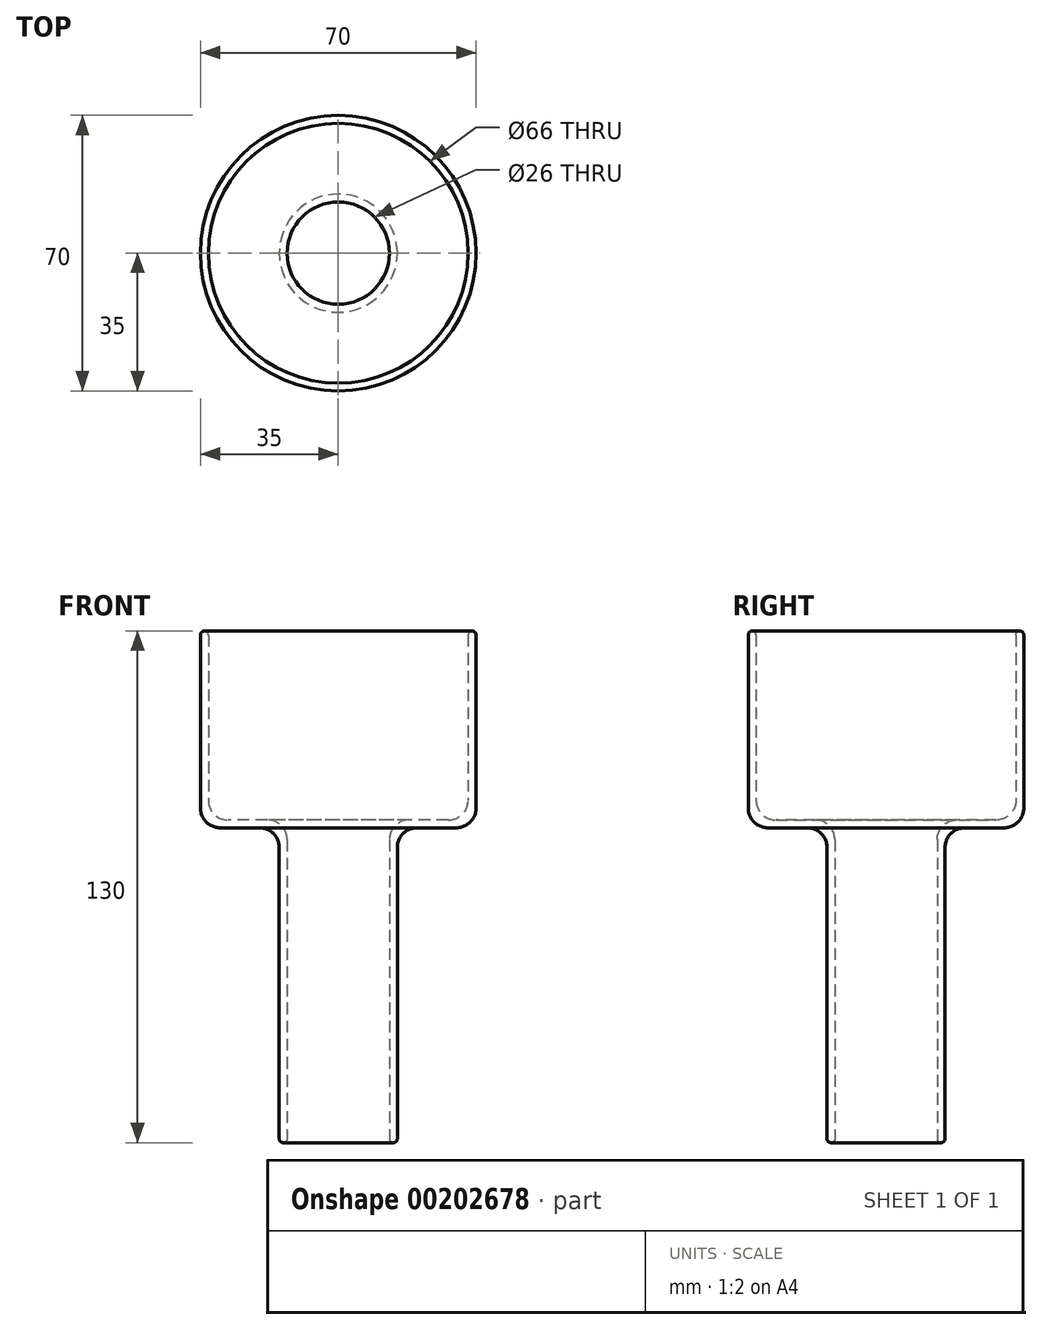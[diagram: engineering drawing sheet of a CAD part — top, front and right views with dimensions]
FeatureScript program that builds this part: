
annotation { "Feature Type Name" : "Feature", "Feature Type Description" : "" }
export const myFeature = defineFeature(function(context is Context, id is Id, definition is map)
    precondition{}
    {
        {
            var Q0;
            Q0=qCreatedBy(makeId("Front.planeOp"),FACE);
            var sketch = newSketch(context, id + "F0", { "sketchPlane" : qUnion([Q0])});
            skLineSegment(sketch, "E0", {"start": v(0, -72.8) * mm, "end": v(0, 57.2) * mm, "construction": true});
            skLineSegment(sketch, "E1", {"start": v(0, 57.2) * mm, "end": v(-35, 57.2) * mm, "construction": true});
            skLineSegment(sketch, "E2", {"start": v(-35, 57.2) * mm, "end": v(-35, 7.2) * mm});
            skLineSegment(sketch, "E3", {"start": v(-35, 7.2) * mm, "end": v(-15, 7.2) * mm});
            skLineSegment(sketch, "E4", {"start": v(-15, 7.2) * mm, "end": v(-15, -72.8) * mm});
            skLineSegment(sketch, "E5", {"start": v(-15, -72.8) * mm, "end": v(0, -72.8) * mm, "construction": true});
            skLineSegment(sketch, "E6.0", {"start": v(-13, 9.2) * mm, "end": v(-13, -72.8) * mm});
            skLineSegment(sketch, "E6.1", {"start": v(-33, 9.2) * mm, "end": v(-13, 9.2) * mm});
            skLineSegment(sketch, "E6.2", {"start": v(-33, 57.2) * mm, "end": v(-33, 9.2) * mm});
            skLineSegment(sketch, "E7", {"start": v(-35, 57.2) * mm, "end": v(-33, 57.2) * mm});
            skLineSegment(sketch, "E8", {"start": v(-15, -72.8) * mm, "end": v(-13, -72.8) * mm});
            skSolve(sketch);
        }
        {
            var Q0;
            Q0 = qSketchRegion(id + "F0", true);
            var Q1;
            Q1=sQuery(id+"F0.wireOp",EDGE,"E0");
            revolve(context, id + "F1", {"entities" : qUnion([Q0]), "axis" : qUnion([Q1]), "revolveType" : RevolveType.FULL});
        }
        {
            var Q0;
            Q0=makeQuery(id+"F1.opRevolve","SWEPT_EDGE",EDGE,{"disambiguationData":[OSD([sQuery(id+"F0.wireOp",EDGE,"E2"),sQuery(id+"F0.wireOp",EDGE,"E7")])]});
            var Q1;
            Q1=makeQuery(id+"F1.opRevolve","SWEPT_EDGE",EDGE,{"disambiguationData":[OSD([sQuery(id+"F0.wireOp",EDGE,"E6.2"),sQuery(id+"F0.wireOp",EDGE,"E7")])]});
            var Q2;
            Q2=makeQuery(id+"F1.opRevolve","SWEPT_FACE",FACE,{"disambiguationData":[OSD([sQuery(id+"F0.wireOp",EDGE,"E8")])]});
            fillet(context, id + "F2", {"entities" : qUnion([Q0, Q1, Q2]), "radius" : 1 * mm, "tangentPropagation" : true, "allowEdgeOverflow" : false});
        }
        {
            var Q0;
            Q0=makeQuery(id+"F1.opRevolve","SWEPT_EDGE",EDGE,{"disambiguationData":[OSD([sQuery(id+"F0.wireOp",EDGE,"E3"),sQuery(id+"F0.wireOp",EDGE,"E4")])]});
            var Q1;
            Q1=makeQuery(id+"F1.opRevolve","SWEPT_EDGE",EDGE,{"disambiguationData":[OSD([sQuery(id+"F0.wireOp",EDGE,"E2"),sQuery(id+"F0.wireOp",EDGE,"E3")])]});
            fillet(context, id + "F3", {"entities" : qUnion([Q0, Q1]), "radius" : 5 * mm, "tangentPropagation" : true, "allowEdgeOverflow" : false});
        }
        {
            var Q0;
            Q0=makeQuery(id+"F1.opRevolve","SWEPT_EDGE",EDGE,{"disambiguationData":[OSD([sQuery(id+"F0.wireOp",EDGE,"E6.0"),sQuery(id+"F0.wireOp",EDGE,"E6.1")])]});
            var Q1;
            Q1=makeQuery(id+"F1.opRevolve","SWEPT_EDGE",EDGE,{"disambiguationData":[OSD([sQuery(id+"F0.wireOp",EDGE,"E6.1"),sQuery(id+"F0.wireOp",EDGE,"E6.2")])]});
            fillet(context, id + "F4", {"entities" : qUnion([Q0, Q1]), "radius" : 5 * mm, "tangentPropagation" : true, "allowEdgeOverflow" : false});
        }
    });
